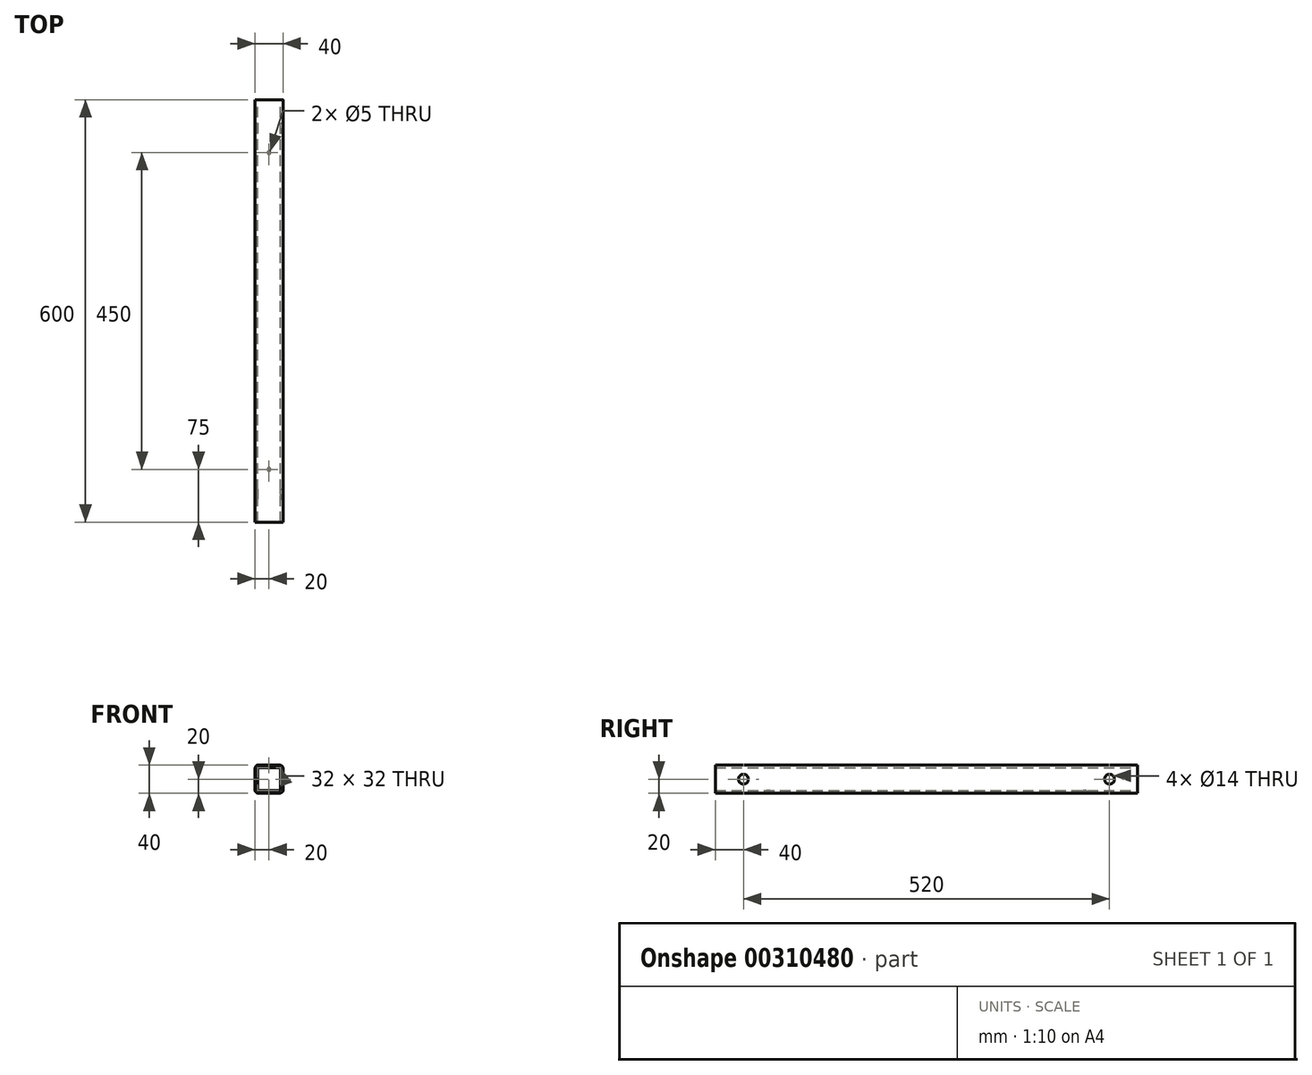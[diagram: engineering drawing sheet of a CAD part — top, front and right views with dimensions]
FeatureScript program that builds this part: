
annotation { "Feature Type Name" : "Feature", "Feature Type Description" : "" }
export const myFeature = defineFeature(function(context is Context, id is Id, definition is map)
    precondition{}
    {
        {
            var Q0;
            Q0=qCreatedBy(makeId("Front.planeOp"),FACE);
            var sketch = newSketch(context, id + "F0", { "sketchPlane" : qUnion([Q0])});
            skLineSegment(sketch, "E0.bottom", {"start": v(15, -20) * mm, "end": v(-15, -20) * mm});
            skLineSegment(sketch, "E0.top", {"start": v(15, 20) * mm, "end": v(-15, 20) * mm});
            skLineSegment(sketch, "E0.left", {"start": v(20, -15) * mm, "end": v(20, 15) * mm});
            skLineSegment(sketch, "E0.right", {"start": v(-20, -15) * mm, "end": v(-20, 15) * mm});
            skPoint(sketch, "E0.middle", {"position": v(0, 0) * mm});
            skPoint(sketch, "E1.visualSharp", {"position": v(-20, 20) * mm});
            skArc(sketch, "E1.filletArc", {"start": v(-15, 20) * mm, "mid": v(-18.54, 18.54) * mm, "end": v(-20, 15) * mm});
            skPoint(sketch, "E2.visualSharp", {"position": v(20, 20) * mm});
            skArc(sketch, "E2.filletArc", {"start": v(20, 15) * mm, "mid": v(18.54, 18.54) * mm, "end": v(15, 20) * mm});
            skPoint(sketch, "E3.visualSharp", {"position": v(20, -20) * mm});
            skArc(sketch, "E3.filletArc", {"start": v(15, -20) * mm, "mid": v(18.54, -18.54) * mm, "end": v(20, -15) * mm});
            skPoint(sketch, "E4.visualSharp", {"position": v(-20, -20) * mm});
            skArc(sketch, "E4.filletArc", {"start": v(-20, -15) * mm, "mid": v(-18.54, -18.54) * mm, "end": v(-15, -20) * mm});
            skLineSegment(sketch, "E5.0", {"start": v(-16, -16) * mm, "end": v(-16, 16) * mm});
            skLineSegment(sketch, "E5.1", {"start": v(16, -16) * mm, "end": v(-16, -16) * mm});
            skLineSegment(sketch, "E5.2", {"start": v(16, -16) * mm, "end": v(16, 16) * mm});
            skLineSegment(sketch, "E5.3", {"start": v(16, 16) * mm, "end": v(-16, 16) * mm});
            skSolve(sketch);
        }
        {
            var Q0;
            Q0=makeQuery(id+"F0.imprint","IMPRINT",FACE,{"disambiguationData":[TD([[makeQuery(id+"F0.imprint","IMPRINT",EDGE,{"derivedFrom":sQuery(id+"F0.wireOp",EDGE,"E0.bottom")}),-1.0]])]});
            extrude(context, id + "F1", {"entities" : qUnion([Q0]), "depth" : 600 * mm});
        }
        {
            var Q0;
            Q0=makeQuery(id+"F1.opExtrude","SWEPT_FACE",FACE,{"disambiguationData":[OSD([sQuery(id+"F0.wireOp",EDGE,"E0.left")])]});
            var sketch = newSketch(context, id + "F2", { "sketchPlane" : qUnion([Q0])});
            skCircle(sketch, "E6", {"center": v(-560, 0) * mm, "radius": 10 * mm});
            skCircle(sketch, "E7", {"center": v(-40, 0) * mm, "radius": 10 * mm});
            skSolve(sketch);
        }
        {
            var Q0;
            Q0=sQuery(id+"F2.wireOp",VERTEX,"E6.center");
            var Q1;
            Q1=makeQuery(id+"F1.opExtrude","SWEPT_BODY",BODY,{"disambiguationData":[OSD([sQuery(id+"F0.wireOp",EDGE,"E0.bottom"),sQuery(id+"F0.wireOp",EDGE,"E0.top"),sQuery(id+"F0.wireOp",EDGE,"E0.left"),sQuery(id+"F0.wireOp",EDGE,"E0.right"),sQuery(id+"F0.wireOp",EDGE,"E1.filletArc"),sQuery(id+"F0.wireOp",EDGE,"E2.filletArc"),sQuery(id+"F0.wireOp",EDGE,"E3.filletArc"),sQuery(id+"F0.wireOp",EDGE,"E4.filletArc"),sQuery(id+"F0.wireOp",EDGE,"E5.0"),sQuery(id+"F0.wireOp",EDGE,"E5.1"),sQuery(id+"F0.wireOp",EDGE,"E5.2"),sQuery(id+"F0.wireOp",EDGE,"E5.3")])]});
            hole(context, id + "F3", {"style" : HoleStyle.SIMPLE, "endStyle" : HoleEndStyle.BLIND, "holeDiameter" : 14 * mm, "holeDepth" : 45 * mm, "tappedDepth" : 12 * mm, "tapClearance" : 3, "startFromSketch" : true, "locations" : qUnion([Q0]), "scope" : qUnion([Q1])});
        }
        {
            var Q0;
            Q0=sQuery(id+"F2.wireOp",VERTEX,"E7.center");
            var Q1;
            Q1=makeQuery(id+"F1.opExtrude","SWEPT_BODY",BODY,{"disambiguationData":[OSD([sQuery(id+"F0.wireOp",EDGE,"E0.bottom"),sQuery(id+"F0.wireOp",EDGE,"E0.top"),sQuery(id+"F0.wireOp",EDGE,"E0.left"),sQuery(id+"F0.wireOp",EDGE,"E0.right"),sQuery(id+"F0.wireOp",EDGE,"E1.filletArc"),sQuery(id+"F0.wireOp",EDGE,"E2.filletArc"),sQuery(id+"F0.wireOp",EDGE,"E3.filletArc"),sQuery(id+"F0.wireOp",EDGE,"E4.filletArc"),sQuery(id+"F0.wireOp",EDGE,"E5.0"),sQuery(id+"F0.wireOp",EDGE,"E5.1"),sQuery(id+"F0.wireOp",EDGE,"E5.2"),sQuery(id+"F0.wireOp",EDGE,"E5.3")])]});
            hole(context, id + "F4", {"style" : HoleStyle.SIMPLE, "endStyle" : HoleEndStyle.BLIND, "holeDiameter" : 14 * mm, "holeDepth" : 45 * mm, "tappedDepth" : 12 * mm, "tapClearance" : 3, "startFromSketch" : true, "locations" : qUnion([Q0]), "scope" : qUnion([Q1])});
        }
        {
            var Q0;
            Q0=makeQuery(id+"F1.opExtrude","SWEPT_FACE",FACE,{"disambiguationData":[OSD([sQuery(id+"F0.wireOp",EDGE,"E0.bottom")])]});
            var sketch = newSketch(context, id + "F5", { "sketchPlane" : qUnion([Q0])});
            skLineSegment(sketch, "E8.bottom", {"start": v(-15, 75) * mm, "end": v(15, 75) * mm});
            skLineSegment(sketch, "E8.top", {"start": v(-15, 525) * mm, "end": v(15, 525) * mm});
            skLineSegment(sketch, "E8.left", {"start": v(-15, 75) * mm, "end": v(-15, 525) * mm});
            skLineSegment(sketch, "E8.right", {"start": v(15, 75) * mm, "end": v(15, 525) * mm});
            skPoint(sketch, "E8.middle", {"position": v(0, 300) * mm});
            skLineSegment(sketch, "E9", {"start": v(0, 600) * mm, "end": v(0, 0) * mm});
            skCircle(sketch, "E10", {"center": v(0, 525) * mm, "radius": 5 * mm});
            skCircle(sketch, "E11", {"center": v(0, 75) * mm, "radius": 5 * mm});
            skSolve(sketch);
        }
        {
            var Q0;
            Q0=sQuery(id+"F5.wireOp",VERTEX,"E10.center");
            var Q1;
            Q1=makeQuery(id+"F1.opExtrude","SWEPT_BODY",BODY,{"disambiguationData":[OSD([sQuery(id+"F0.wireOp",EDGE,"E0.bottom"),sQuery(id+"F0.wireOp",EDGE,"E0.top"),sQuery(id+"F0.wireOp",EDGE,"E0.left"),sQuery(id+"F0.wireOp",EDGE,"E0.right"),sQuery(id+"F0.wireOp",EDGE,"E1.filletArc"),sQuery(id+"F0.wireOp",EDGE,"E2.filletArc"),sQuery(id+"F0.wireOp",EDGE,"E3.filletArc"),sQuery(id+"F0.wireOp",EDGE,"E4.filletArc"),sQuery(id+"F0.wireOp",EDGE,"E5.0"),sQuery(id+"F0.wireOp",EDGE,"E5.1"),sQuery(id+"F0.wireOp",EDGE,"E5.2"),sQuery(id+"F0.wireOp",EDGE,"E5.3")])]});
            hole(context, id + "F6", {"style" : HoleStyle.SIMPLE, "endStyle" : HoleEndStyle.BLIND, "holeDiameter" : 5 * mm, "holeDepth" : 5 * mm, "tappedDepth" : 12 * mm, "tapClearance" : 3, "startFromSketch" : true, "locations" : qUnion([Q0]), "scope" : qUnion([Q1])});
        }
        {
            var Q0;
            Q0=sQuery(id+"F5.wireOp",VERTEX,"E11.center");
            var Q1;
            Q1=makeQuery(id+"F1.opExtrude","SWEPT_BODY",BODY,{"disambiguationData":[OSD([sQuery(id+"F0.wireOp",EDGE,"E0.bottom"),sQuery(id+"F0.wireOp",EDGE,"E0.top"),sQuery(id+"F0.wireOp",EDGE,"E0.left"),sQuery(id+"F0.wireOp",EDGE,"E0.right"),sQuery(id+"F0.wireOp",EDGE,"E1.filletArc"),sQuery(id+"F0.wireOp",EDGE,"E2.filletArc"),sQuery(id+"F0.wireOp",EDGE,"E3.filletArc"),sQuery(id+"F0.wireOp",EDGE,"E4.filletArc"),sQuery(id+"F0.wireOp",EDGE,"E5.0"),sQuery(id+"F0.wireOp",EDGE,"E5.1"),sQuery(id+"F0.wireOp",EDGE,"E5.2"),sQuery(id+"F0.wireOp",EDGE,"E5.3")])]});
            hole(context, id + "F7", {"style" : HoleStyle.SIMPLE, "endStyle" : HoleEndStyle.BLIND, "holeDiameter" : 5 * mm, "holeDepth" : 5 * mm, "tappedDepth" : 12 * mm, "tapClearance" : 3, "startFromSketch" : true, "locations" : qUnion([Q0]), "scope" : qUnion([Q1])});
        }
    });
